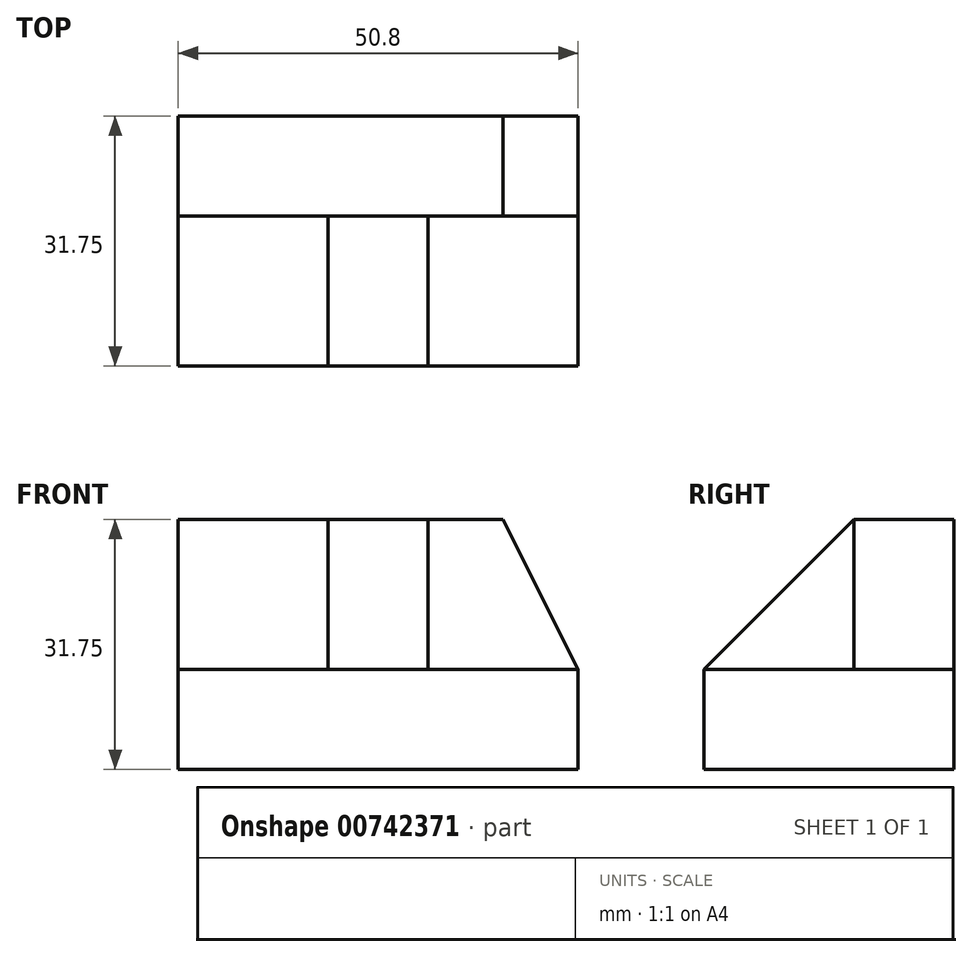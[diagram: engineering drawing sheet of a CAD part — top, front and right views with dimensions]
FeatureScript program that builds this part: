
annotation { "Feature Type Name" : "Feature", "Feature Type Description" : "" }
export const myFeature = defineFeature(function(context is Context, id is Id, definition is map)
    precondition{}
    {
        {
            var Q0;
            Q0=qCreatedBy(makeId("Front.planeOp"),FACE);
            var sketch = newSketch(context, id + "F0", { "sketchPlane" : qUnion([Q0])});
            skLineSegment(sketch, "E0.bottom", {"start": v(0, 0) * mm, "end": v(-50.8, 0) * mm});
            skLineSegment(sketch, "E0.top", {"start": v(0, 31.75) * mm, "end": v(-50.8, 31.75) * mm});
            skLineSegment(sketch, "E0.left", {"start": v(0, 0) * mm, "end": v(0, 31.75) * mm});
            skLineSegment(sketch, "E0.right", {"start": v(-50.8, 0) * mm, "end": v(-50.8, 31.75) * mm});
            skSolve(sketch);
        }
        {
            var Q0;
            Q0=makeQuery(id+"F0.imprint","IMPRINT",FACE,{"disambiguationData":[TD([[makeQuery(id+"F0.imprint","IMPRINT",EDGE,{"derivedFrom":sQuery(id+"F0.wireOp",EDGE,"E0.bottom")}),-1.0]])]});
            extrude(context, id + "F1", {"entities" : qUnion([Q0]), "depth" : 31.75 * mm, "offsetDistance" : 25.4 * mm});
        }
        {
            var Q0;
            Q0=makeQuery(id+"F1.opExtrude","CAP_FACE",FACE,{"disambiguationData":[OSD([sQuery(id+"F0.wireOp",EDGE,"E0.bottom"),sQuery(id+"F0.wireOp",EDGE,"E0.top"),sQuery(id+"F0.wireOp",EDGE,"E0.left"),sQuery(id+"F0.wireOp",EDGE,"E0.right")])],"isStart":false});
            var sketch = newSketch(context, id + "F2", { "sketchPlane" : qUnion([Q0])});
            skLineSegment(sketch, "E1.bottom", {"start": v(-31.75, 12.7) * mm, "end": v(-50.8, 12.7) * mm});
            skLineSegment(sketch, "E1.top", {"start": v(-31.75, 31.75) * mm, "end": v(-50.8, 31.75) * mm});
            skLineSegment(sketch, "E1.left", {"start": v(-31.75, 12.7) * mm, "end": v(-31.75, 31.75) * mm});
            skLineSegment(sketch, "E1.right", {"start": v(-50.8, 12.7) * mm, "end": v(-50.8, 31.75) * mm});
            skSolve(sketch);
        }
        {
            var Q0;
            Q0=makeQuery(id+"F2.imprint","IMPRINT",FACE,{"disambiguationData":[TD([[makeQuery(id+"F2.imprint","IMPRINT",EDGE,{"derivedFrom":sQuery(id+"F2.wireOp",EDGE,"E1.bottom")}),-1.0]])]});
            extrude(context, id + "F3", {"entities" : qUnion([Q0]), "operationType" : NewBodyOperationType.REMOVE, "oppositeDirection" : true, "depth" : 19.05 * mm, "offsetDistance" : 25.4 * mm});
        }
        {
            var Q0;
            Q0=makeQuery(id+"F1.opExtrude","CAP_FACE",FACE,{"disambiguationData":[OSD([sQuery(id+"F0.wireOp",EDGE,"E0.bottom"),sQuery(id+"F0.wireOp",EDGE,"E0.top"),sQuery(id+"F0.wireOp",EDGE,"E0.left"),sQuery(id+"F0.wireOp",EDGE,"E0.right")])],"isStart":false});
            var sketch = newSketch(context, id + "F4", { "sketchPlane" : qUnion([Q0])});
            skLineSegment(sketch, "E2.bottom", {"start": v(0, 31.75) * mm, "end": v(-19.05, 31.75) * mm});
            skLineSegment(sketch, "E2.top", {"start": v(0, 12.7) * mm, "end": v(-19.05, 12.7) * mm});
            skLineSegment(sketch, "E2.left", {"start": v(0, 31.75) * mm, "end": v(0, 12.7) * mm});
            skLineSegment(sketch, "E2.right", {"start": v(-19.05, 31.75) * mm, "end": v(-19.05, 12.7) * mm});
            skSolve(sketch);
        }
        {
            var Q0;
            Q0=makeQuery(id+"F4.imprint","IMPRINT",FACE,{"disambiguationData":[TD([[makeQuery(id+"F4.imprint","IMPRINT",EDGE,{"derivedFrom":sQuery(id+"F4.wireOp",EDGE,"E2.bottom")}),1.0]])]});
            extrude(context, id + "F5", {"entities" : qUnion([Q0]), "operationType" : NewBodyOperationType.REMOVE, "oppositeDirection" : true, "depth" : 19.05 * mm, "offsetDistance" : 25.4 * mm});
        }
        {
            var Q0;
            Q0=makeQuery(id+"F5.boolean.opBoolean","COPY",FACE,{"derivedFrom":makeQuery(id+"F5.opExtrude","CAP_FACE",FACE,{"disambiguationData":[OSD([sQuery(id+"F4.wireOp",EDGE,"E2.bottom"),sQuery(id+"F4.wireOp",EDGE,"E2.top"),sQuery(id+"F4.wireOp",EDGE,"E2.left"),sQuery(id+"F4.wireOp",EDGE,"E2.right")])],"isStart":false})});
            var sketch = newSketch(context, id + "F6", { "sketchPlane" : qUnion([Q0])});
            skLineSegment(sketch, "E3", {"start": v(0, 12.7) * mm, "end": v(-9.53, 31.75) * mm});
            skSolve(sketch);
        }
        {
            var Q0;
            {var subQ0=sQuery(id+"F6.wireOp",EDGE,"E3");Q0=makeQuery(id+"F6.imprint","IMPRINT",FACE,{"disambiguationData":[TD([[makeQuery(id+"F6.imprint","IMPRINT",EDGE,{"derivedFrom":subQ0}),-1.0]])]});}
            extrude(context, id + "F7", {"entities" : qUnion([Q0]), "operationType" : NewBodyOperationType.REMOVE, "endBound" : BoundingType.THROUGH_ALL, "oppositeDirection" : true, "depth" : 25.4 * mm, "offsetDistance" : 25.4 * mm});
        }
        {
            var Q0;
            Q0=makeQuery(id+"F5.boolean.opBoolean","COPY",FACE,{"derivedFrom":makeQuery(id+"F5.opExtrude","SWEPT_FACE",FACE,{"disambiguationData":[OSD([sQuery(id+"F4.wireOp",EDGE,"E2.right")])]})});
            var sketch = newSketch(context, id + "F8", { "sketchPlane" : qUnion([Q0])});
            skLineSegment(sketch, "E4", {"start": v(-12.7, 31.75) * mm, "end": v(-31.75, 12.7) * mm});
            skSolve(sketch);
        }
        {
            var Q0;
            Q0=makeQuery(id+"F8.imprint","IMPRINT",FACE,{"disambiguationData":[TD([[makeQuery(id+"F8.imprint","IMPRINT",EDGE,{"derivedFrom":sQuery(id+"F8.wireOp",EDGE,"E4")}),-1.0]])]});
            extrude(context, id + "F9", {"entities" : qUnion([Q0]), "operationType" : NewBodyOperationType.REMOVE, "endBound" : BoundingType.THROUGH_ALL, "oppositeDirection" : true, "depth" : 25.4 * mm, "offsetDistance" : 25.4 * mm});
        }
    });
